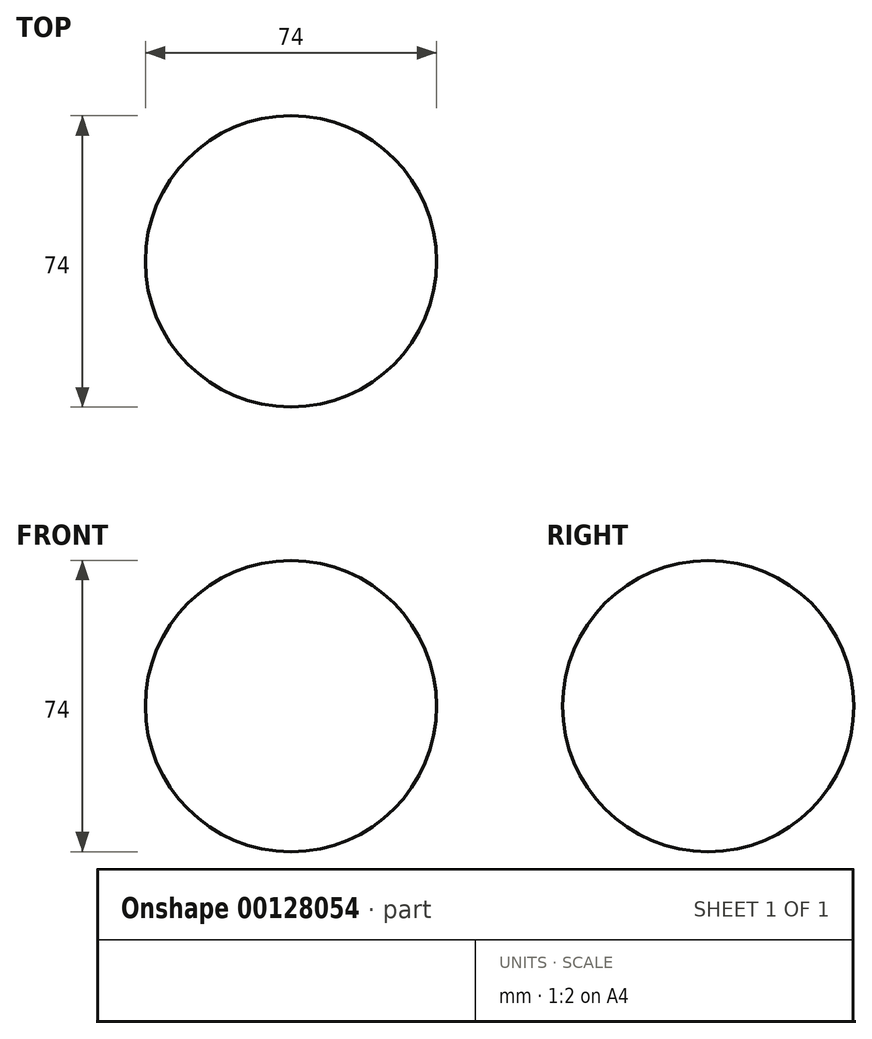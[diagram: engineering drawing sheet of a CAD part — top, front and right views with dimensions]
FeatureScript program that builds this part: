
annotation { "Feature Type Name" : "Feature", "Feature Type Description" : "" }
export const myFeature = defineFeature(function(context is Context, id is Id, definition is map)
    precondition{}
    {
        {
            var Q0;
            Q0=qCreatedBy(makeId("Top.planeOp"),FACE);
            var sketch = newSketch(context, id + "F0", { "sketchPlane" : qUnion([Q0])});
            skArc(sketch, "E0", {"start": v(0, -37) * mm, "mid": v(37, 0) * mm, "end": v(0, 37) * mm});
            skLineSegment(sketch, "E1", {"start": v(0, 37) * mm, "end": v(0, -37) * mm});
            skSolve(sketch);
        }
        {
            var Q0;
            Q0 = qSketchRegion(id + "F0", true);
            var Q1;
            Q1=sQuery(id+"F0.wireOp",EDGE,"E1");
            revolve(context, id + "F1", {"entities" : qUnion([Q0]), "axis" : qUnion([Q1]), "revolveType" : RevolveType.FULL});
        }
    });
